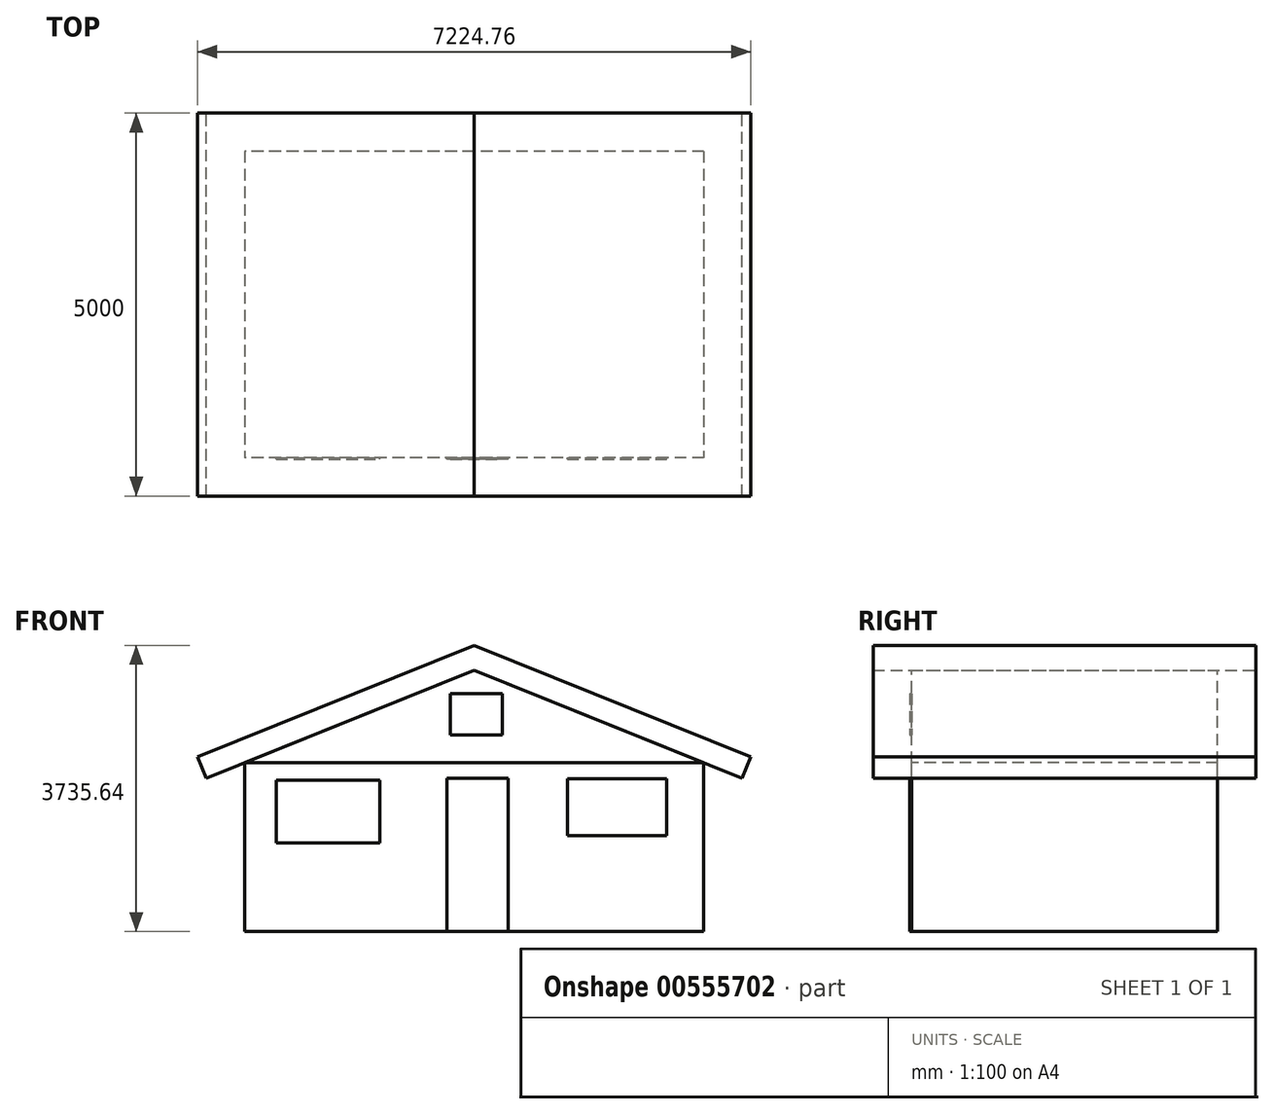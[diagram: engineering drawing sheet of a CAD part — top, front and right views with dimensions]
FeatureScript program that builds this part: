
annotation { "Feature Type Name" : "Feature", "Feature Type Description" : "" }
export const myFeature = defineFeature(function(context is Context, id is Id, definition is map)
    precondition{}
    {
        {
            var Q0;
            Q0=qCreatedBy(makeId("Front.planeOp"),FACE);
            var sketch = newSketch(context, id + "F0", { "sketchPlane" : qUnion([Q0])});
            skLineSegment(sketch, "E0", {"start": v(4364.47, 0) * mm, "end": v(4364.47, 2200) * mm});
            skLineSegment(sketch, "E1", {"start": v(4364.47, 0) * mm, "end": v(-1635.53, 0) * mm});
            skLineSegment(sketch, "E2", {"start": v(-1635.53, 0) * mm, "end": v(-1635.53, 2200) * mm});
            skLineSegment(sketch, "E3", {"start": v(-1635.53, 2200) * mm, "end": v(4364.47, 2200) * mm});
            skSolve(sketch);
        }
        {
            var Q0;
            Q0 = qSketchRegion(id + "F0", true);
            extrude(context, id + "F1", {"entities" : qUnion([Q0]), "oppositeDirection" : true, "depth" : 4000 * mm, "offsetDistance" : 25 * mm});
        }
        {
            var Q0;
            Q0=makeQuery(id+"F1.opExtrude","CAP_FACE",FACE,{"disambiguationData":[OSD([sQuery(id+"F0.wireOp",EDGE,"E0"),sQuery(id+"F0.wireOp",EDGE,"E1"),sQuery(id+"F0.wireOp",EDGE,"E2"),sQuery(id+"F0.wireOp",EDGE,"E3")])],"isStart":true});
            var sketch = newSketch(context, id + "F2", { "sketchPlane" : qUnion([Q0])});
            skLineSegment(sketch, "E4", {"start": v(-2135.53, 1997.99) * mm, "end": v(1364.47, 3412.08) * mm});
            skLineSegment(sketch, "E5", {"start": v(1364.47, 3412.08) * mm, "end": v(4864.47, 1997.99) * mm});
            skLineSegment(sketch, "E6", {"start": v(4864.47, 1997.99) * mm, "end": v(4976.85, 2276.14) * mm});
            skLineSegment(sketch, "E7", {"start": v(4976.85, 2276.14) * mm, "end": v(1364.47, 3735.64) * mm});
            skLineSegment(sketch, "E8", {"start": v(1364.47, 3735.64) * mm, "end": v(-2247.91, 2276.14) * mm});
            skLineSegment(sketch, "E9", {"start": v(-2247.91, 2276.14) * mm, "end": v(-2135.53, 1997.99) * mm});
            skSolve(sketch);
        }
        {
            var Q0;
            Q0 = qSketchRegion(id + "F2", true);
            extrude(context, id + "F3", {"entities" : qUnion([Q0]), "depth" : 500 * mm, "offsetDistance" : 25 * mm});
        }
        {
            var Q0;
            Q0=makeQuery(id+"F3.opExtrude","CAP_FACE",FACE,{"disambiguationData":[OSD([sQuery(id+"F2.wireOp",EDGE,"E4"),sQuery(id+"F2.wireOp",EDGE,"E5"),sQuery(id+"F2.wireOp",EDGE,"E6"),sQuery(id+"F2.wireOp",EDGE,"E7"),sQuery(id+"F2.wireOp",EDGE,"E8"),sQuery(id+"F2.wireOp",EDGE,"E9")])],"isStart":true});
            extrude(context, id + "F4", {"entities" : qUnion([Q0]), "operationType" : NewBodyOperationType.ADD, "depth" : 4500 * mm, "offsetDistance" : 25 * mm});
        }
        {
            var Q0;
            Q0=makeQuery(id+"F1.opExtrude","CAP_FACE",FACE,{"disambiguationData":[OSD([sQuery(id+"F0.wireOp",EDGE,"E0"),sQuery(id+"F0.wireOp",EDGE,"E1"),sQuery(id+"F0.wireOp",EDGE,"E2"),sQuery(id+"F0.wireOp",EDGE,"E3")])],"isStart":false});
            var sketch = newSketch(context, id + "F5", { "sketchPlane" : qUnion([Q0])});
            skLineSegment(sketch, "E10", {"start": v(-4364.47, 2200) * mm, "end": v(-1364.47, 3412.08) * mm});
            skLineSegment(sketch, "E11", {"start": v(-1364.47, 3412.08) * mm, "end": v(1635.53, 2200) * mm});
            skLineSegment(sketch, "E12", {"start": v(1635.53, 2200) * mm, "end": v(-4364.47, 2200) * mm});
            skSolve(sketch);
        }
        {
            var Q0;
            Q0=makeQuery(id+"F5.imprint","IMPRINT",FACE,{"disambiguationData":[TD([[makeQuery(id+"F5.imprint","IMPRINT",EDGE,{"derivedFrom":sQuery(id+"F5.wireOp",EDGE,"E10")}),-1.0]])]});
            extrude(context, id + "F6", {"entities" : qUnion([Q0]), "oppositeDirection" : true, "depth" : 4000 * mm, "offsetDistance" : 25 * mm});
        }
        {
            var Q0;
            Q0=makeQuery(id+"F1.opExtrude","CAP_FACE",FACE,{"disambiguationData":[OSD([sQuery(id+"F0.wireOp",EDGE,"E0"),sQuery(id+"F0.wireOp",EDGE,"E1"),sQuery(id+"F0.wireOp",EDGE,"E2"),sQuery(id+"F0.wireOp",EDGE,"E3")])],"isStart":true});
            var sketch = newSketch(context, id + "F7", { "sketchPlane" : qUnion([Q0])});
            skLineSegment(sketch, "E13.bottom", {"start": v(1011.83, 0) * mm, "end": v(1811.83, 0) * mm});
            skLineSegment(sketch, "E13.top", {"start": v(1011.83, 2000) * mm, "end": v(1811.83, 2000) * mm});
            skLineSegment(sketch, "E13.left", {"start": v(1011.83, 0) * mm, "end": v(1011.83, 2000) * mm});
            skLineSegment(sketch, "E13.right", {"start": v(1811.83, 0) * mm, "end": v(1811.83, 2000) * mm});
            skLineSegment(sketch, "E14.bottom", {"start": v(1055.68, 3107.36) * mm, "end": v(1729.6, 3107.36) * mm});
            skLineSegment(sketch, "E14.top", {"start": v(1055.68, 2563.88) * mm, "end": v(1729.6, 2563.88) * mm});
            skLineSegment(sketch, "E14.left", {"start": v(1055.68, 3107.36) * mm, "end": v(1055.68, 2563.88) * mm});
            skLineSegment(sketch, "E14.right", {"start": v(1729.6, 3107.36) * mm, "end": v(1729.6, 2563.88) * mm});
            skLineSegment(sketch, "E15.bottom", {"start": v(-1222.88, 1975.42) * mm, "end": v(131, 1975.42) * mm});
            skLineSegment(sketch, "E15.top", {"start": v(-1222.88, 1157.53) * mm, "end": v(131, 1157.53) * mm});
            skLineSegment(sketch, "E15.left", {"start": v(-1222.88, 1975.42) * mm, "end": v(-1222.88, 1157.53) * mm});
            skLineSegment(sketch, "E15.right", {"start": v(131, 1975.42) * mm, "end": v(131, 1157.53) * mm});
            skLineSegment(sketch, "E16.bottom", {"start": v(2580.75, 1991.62) * mm, "end": v(3877.05, 1991.62) * mm});
            skLineSegment(sketch, "E16.top", {"start": v(2580.75, 1250.6) * mm, "end": v(3877.05, 1250.6) * mm});
            skLineSegment(sketch, "E16.left", {"start": v(2580.75, 1991.62) * mm, "end": v(2580.75, 1250.6) * mm});
            skLineSegment(sketch, "E16.right", {"start": v(3877.05, 1991.62) * mm, "end": v(3877.05, 1250.6) * mm});
            skSolve(sketch);
        }
        {
            var Q0;
            Q0=makeQuery(id+"F7.imprint","IMPRINT",FACE,{"disambiguationData":[TD([[makeQuery(id+"F7.imprint","IMPRINT",EDGE,{"derivedFrom":sQuery(id+"F7.wireOp",EDGE,"E13.bottom")}),-1.0]])]});
            var Q1;
            Q1=makeQuery(id+"F7.imprint","IMPRINT",FACE,{"disambiguationData":[TD([[makeQuery(id+"F7.imprint","IMPRINT",EDGE,{"derivedFrom":sQuery(id+"F7.wireOp",EDGE,"E16.bottom")}),-1.0]])]});
            var Q2;
            Q2=makeQuery(id+"F7.imprint","IMPRINT",FACE,{"disambiguationData":[TD([[makeQuery(id+"F7.imprint","IMPRINT",EDGE,{"derivedFrom":sQuery(id+"F7.wireOp",EDGE,"E15.bottom")}),-1.0]])]});
            var Q3;
            Q3=makeQuery(id+"F7.imprint","IMPRINT",FACE,{"disambiguationData":[TD([[makeQuery(id+"F7.imprint","IMPRINT",EDGE,{"derivedFrom":sQuery(id+"F7.wireOp",EDGE,"E14.bottom")}),-1.0]])]});
            extrude(context, id + "F8", {"entities" : qUnion([Q0, Q1, Q2, Q3]), "depth" : 22 * mm, "offsetDistance" : 25 * mm});
        }
    });
